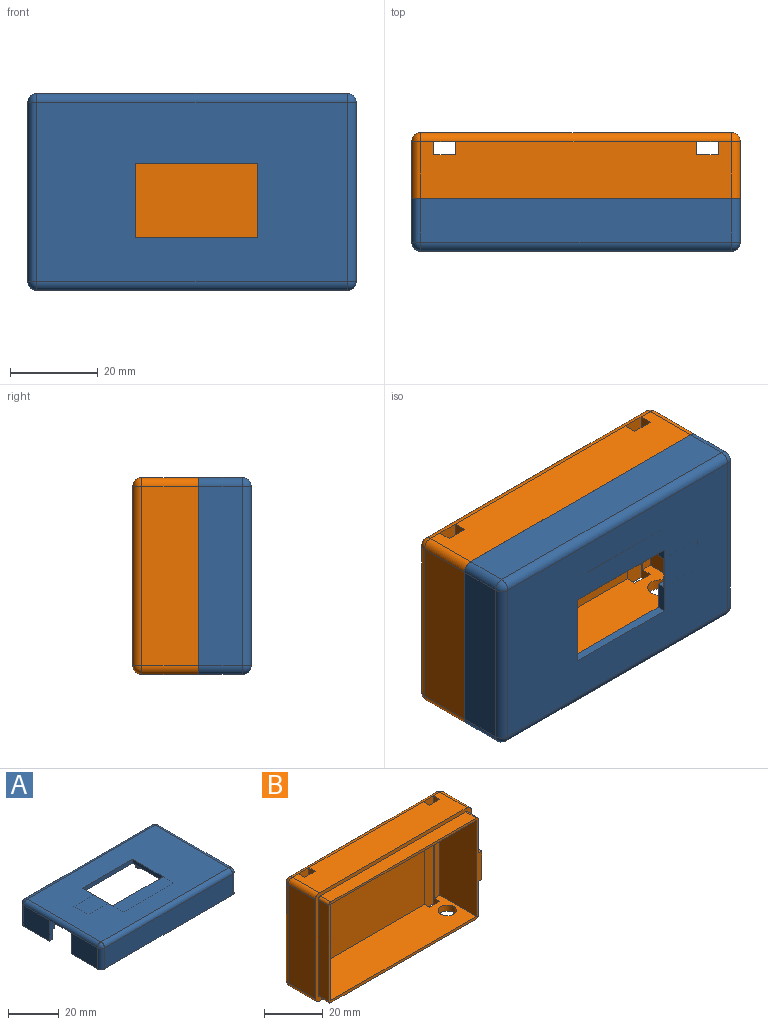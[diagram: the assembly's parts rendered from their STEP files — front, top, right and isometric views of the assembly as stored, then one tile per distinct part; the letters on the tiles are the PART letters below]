
ASSEMBLY  parts=2 mates=1
PART A: 55 faces, bbox 75x45x12 mm
  f0: cylinder r=2mm len=4mm, axis (0,0,1), area 37.7mm2, adj f12,f54
  f1: cylinder r=2mm len=4mm, axis (0,0,1), area 37.7mm2, adj f12,f53
  f2: cylinder r=2mm len=4mm, axis (0,0,1), area 37.7mm2, adj f12,f52
  f3: cylinder r=2mm len=4mm, axis (0,0,1), area 37.7mm2, adj f12,f51
  f4: plane 14x5mm, normal (1,0,0), area 70mm2, adj f7,f12,f40,f50
  f5: plane 75x45mm, normal (0,0,-1), area 309mm2, adj f10,f16,f17,f18,f19,f27,f29,f32
  f6: plane 14x5mm, normal (1,0,0), area 70mm2, adj f9,f12,f39,f50
  f7: plane 70x5mm, normal (0,1,0), area 350mm2, adj f4,f8,f12,f50
  f8: plane 40x5mm, normal (-1,0,0), area 200mm2, adj f7,f9,f12,f50
  f9: plane 70x5mm, normal (0,-1,0), area 350mm2, adj f6,f8,f12,f50
  f10: plane 14.5x10mm, normal (-1,0,0), area 145mm2, adj f5,f35,f38,f40
  f11: plane 28x0.2mm, normal (0,1,0), area 5.6mm2, adj f13,f15,f20,f26
  f12: plane 72.5x40mm, normal (0,0,-1), area 2047.7mm2, adj f0,f1,f2,f3,f4,f6,f7,f8
  f13: plane 23x2mm, normal (1,0,0), area 30.4mm2, adj f11,f12,f14,f20,f21,f22,f24,f25
  f14: plane 28x2mm, normal (0,-1,0), area 56mm2, adj f12,f13,f15,f20
  f15: plane 23x2mm, normal (-1,0,0), area 44.8mm2, adj f11,f12,f14,f20,f25,f26
  f16: plane 14.5x10mm, normal (-1,0,0), area 145mm2, adj f5,f29,f35,f39
  f17: plane 71x10mm, normal (0,-1,0), area 710mm2, adj f5,f32,f36,f38
  f18: plane 41x10mm, normal (1,0,0), area 410mm2, adj f5,f27,f31,f32
  f19: plane 71x10mm, normal (0,1,0), area 710mm2, adj f5,f27,f29,f30
  f20: plane 71x41mm, normal (0,0,1), area 2435mm2, adj f11,f13,f14,f15,f30,f31,f35,f36
  f21: plane 11x1.8mm, normal (0,-1,0), area 19.8mm2, adj f12,f13,f23,f24
  f22: plane 11x1.8mm, normal (0,1,0), area 19.8mm2, adj f12,f13,f23,f24
  f23: plane 8x1.8mm, normal (1,0,0), area 14.4mm2, adj f12,f21,f22,f24
  f24: plane 11x8mm, normal (0,0,-1), area 88mm2, adj f13,f21,f22,f23
  f25: plane 28x1.8mm, normal (0,1,0), area 50.4mm2, adj f12,f13,f15,f26
  f26: plane 28x6mm, normal (0,0,-1), area 168mm2, adj f11,f13,f15,f25
  f27: cylinder r=2mm len=10mm, axis (0,0,-1), area 31.4mm2, adj f5,f18,f19,f28
  f28: sphere r=2mm, area 6.3mm2, adj f27,f30,f31
  f29: cylinder r=2mm len=10mm, axis (0,0,1), area 31.4mm2, adj f5,f16,f19,f33
  f30: cylinder r=2mm len=71mm, axis (-1,0,0), area 223.1mm2, adj f19,f20,f28,f33
  f31: cylinder r=2mm len=41mm, axis (0,1,0), area 128.8mm2, adj f18,f20,f28,f34
  f32: cylinder r=2mm len=10mm, axis (0,0,1), area 31.4mm2, adj f5,f17,f18,f34
  f33: sphere r=2mm, area 6.3mm2, adj f29,f30,f35
  f34: sphere r=2mm, area 6.3mm2, adj f31,f32,f36
  f35: cylinder r=2mm len=41mm, axis (0,-1,0), area 128.8mm2, adj f10,f12,f16,f20,f33,f37
  f36: cylinder r=2mm len=71mm, axis (1,0,0), area 223.1mm2, adj f17,f20,f34,f37
  f37: sphere r=2mm, area 6.3mm2, adj f35,f36,f38
  f38: cylinder r=2mm len=10mm, axis (0,0,-1), area 31.4mm2, adj f5,f10,f17,f37
  f39: plane 10x2.5mm, normal (0,-1,0), area 19.5mm2, adj f5,f6,f12,f16,f41,f50
  f40: plane 10x2.5mm, normal (0,1,0), area 19.5mm2, adj f4,f5,f10,f12,f49,f50
  f41: plane 14x5mm, normal (1,0,0), area 70mm2, adj f5,f39,f42,f50
  f42: cylinder r=1.1mm len=5mm, axis (0,0,-1), area 8.6mm2, adj f5,f41,f43,f50
  f43: plane 70x5mm, normal (0,-1,0), area 350mm2, adj f5,f42,f44,f50
  f44: cylinder r=1.1mm len=5mm, axis (0,0,-1), area 8.6mm2, adj f5,f43,f45,f50
  f45: plane 40x5mm, normal (-1,0,0), area 200mm2, adj f5,f44,f46,f50
  f46: cylinder r=1.1mm len=5mm, axis (0,0,-1), area 8.6mm2, adj f5,f45,f47,f50
  f47: plane 70x5mm, normal (0,1,0), area 350mm2, adj f5,f46,f48,f50
  f48: cylinder r=1.1mm len=5mm, axis (0,0,-1), area 8.6mm2, adj f5,f47,f49,f50
  f49: plane 14x5mm, normal (1,0,0), area 70mm2, adj f5,f40,f48,f50
  f50: plane 72.2x42.2mm, normal (0,0,-1), area 232.6mm2, adj f4,f6,f7,f8,f9,f39,f40,f41
  f51: plane 4x4mm, normal (0,0,-1), area 12.6mm2, adj f3
  f52: plane 4x4mm, normal (0,0,-1), area 12.6mm2, adj f2
  f53: plane 4x4mm, normal (0,0,-1), area 12.6mm2, adj f1
  f54: plane 4x4mm, normal (0,0,-1), area 12.6mm2, adj f0
PART B: 48 faces, bbox 75x20x45 mm
  f0: plane 55x40mm, normal (0,-1,0), area 2200mm2, adj f7,f9,f28,f35
  f1: plane 40x2.5mm, normal (0,-1,0), area 100mm2, adj f7,f8,f9,f30
  f2: plane 71x13mm, normal (0,0,1), area 893mm2, adj f19,f26,f28,f30,f31,f33,f35,f36
  f3: plane 71x13mm, normal (0,0,-1), area 862.3mm2, adj f19,f25,f27,f28,f30,f32,f33,f35
  f4: plane 13.9x5mm, normal (1,0,0), area 69.5mm2, adj f5,f17,f19,f23
  f5: plane 73.5x42mm, normal (0,-1,0), area 241mm2, adj f4,f6,f7,f8,f9,f11,f12,f13
  f6: plane 40x17.5mm, normal (1,0,0), area 700mm2, adj f5,f7,f9,f10
  f7: plane 70x17.5mm, normal (0,0,1), area 1169.3mm2, adj f0,f1,f5,f6,f8,f10,f25,f27
  f8: plane 40x17.5mm, normal (-1,0,0), area 700mm2, adj f1,f5,f7,f9
  f9: plane 70x17.5mm, normal (0,0,-1), area 1200mm2, adj f0,f1,f5,f6,f8,f10,f26,f28
  f10: plane 40x2.5mm, normal (0,-1,0), area 100mm2, adj f6,f7,f9,f33
  f11: cylinder r=1.1mm len=5mm, axis (0,-1,0), area 8.6mm2, adj f5,f12,f18,f19
  f12: plane 39.8x5mm, normal (-1,0,0), area 199mm2, adj f5,f11,f13,f19
  f13: cylinder r=1.1mm len=5mm, axis (0,-1,0), area 8.6mm2, adj f5,f12,f14,f19
  f14: plane 69.8x5mm, normal (0,0,1), area 349mm2, adj f5,f13,f15,f19
  f15: cylinder r=1.1mm len=5mm, axis (0,-1,0), area 8.6mm2, adj f5,f14,f16,f19
  f16: plane 13.9x5mm, normal (1,0,0), area 69.5mm2, adj f5,f15,f19,f24
  f17: cylinder r=1.1mm len=5mm, axis (0,-1,0), area 8.6mm2, adj f4,f5,f18,f19
  f18: plane 69.8x5mm, normal (0,0,-1), area 349mm2, adj f5,f11,f17,f19
  f19: plane 75x45mm, normal (0,-1,0), area 330.6mm2, adj f2,f3,f4,f11,f12,f13,f14,f15
  f20: plane 71x41mm, normal (0,1,0), area 2911mm2, adj f39,f40,f44,f45
  f21: plane 41x18mm, normal (1,0,0), area 593mm2, adj f5,f19,f23,f24,f36,f38,f39
  f22: plane 41x13mm, normal (-1,0,0), area 533mm2, adj f19,f41,f45,f47
  f23: plane 5x1.5mm, normal (0,0,-1), area 7.5mm2, adj f4,f5,f19,f21
  f24: plane 5x1.5mm, normal (0,0,1), area 7.5mm2, adj f5,f16,f19,f21
  f25: cylinder r=3.12mm len=6.25mm, axis (0,0,-1), area 49.1mm2, adj f3,f7
  f26: plane 5x2.5mm, normal (0,1,0), area 12.5mm2, adj f2,f9,f28,f30
  f27: plane 5x2.5mm, normal (0,1,0), area 12.5mm2, adj f3,f7,f28,f30
  f28: plane 45x3mm, normal (1,0,0), area 35mm2, adj f0,f2,f3,f7,f9,f26,f27,f29
  f29: plane 45x5mm, normal (0,-1,0), area 225mm2, adj f28,f30,f40,f44
  f30: plane 45x3mm, normal (-1,0,0), area 35mm2, adj f1,f2,f3,f7,f9,f26,f27,f29
  f31: plane 5x2.5mm, normal (0,1,0), area 12.5mm2, adj f2,f9,f33,f35
  f32: plane 5x2.5mm, normal (0,1,0), area 12.5mm2, adj f3,f7,f33,f35
  f33: plane 45x3mm, normal (1,0,0), area 35mm2, adj f2,f3,f7,f9,f10,f31,f32,f34
  f34: plane 45x5mm, normal (0,-1,0), area 225mm2, adj f33,f35,f40,f44
  f35: plane 45x3mm, normal (-1,0,0), area 35mm2, adj f0,f2,f3,f7,f9,f31,f32,f34
  f36: cylinder r=2mm len=13mm, axis (0,-1,0), area 40.8mm2, adj f2,f19,f21,f37
  f37: sphere r=2mm, area 6.3mm2, adj f36,f39,f40
  f38: cylinder r=2mm len=13mm, axis (0,1,0), area 40.8mm2, adj f3,f19,f21,f42
  f39: cylinder r=2mm len=41mm, axis (0,0,1), area 128.8mm2, adj f20,f21,f37,f42
  f40: cylinder r=2mm len=71mm, axis (-1,0,0), area 223.1mm2, adj f2,f20,f29,f34,f37,f43
  f41: cylinder r=2mm len=13mm, axis (0,1,0), area 40.8mm2, adj f2,f19,f22,f43
  f42: sphere r=2mm, area 6.3mm2, adj f38,f39,f44
  f43: sphere r=2mm, area 6.3mm2, adj f40,f41,f45
  f44: cylinder r=2mm len=71mm, axis (1,0,0), area 223.1mm2, adj f3,f20,f29,f34,f42,f46
  f45: cylinder r=2mm len=41mm, axis (0,0,-1), area 128.8mm2, adj f20,f22,f43,f46
  f46: sphere r=2mm, area 6.3mm2, adj f44,f45,f47
  f47: cylinder r=2mm len=13mm, axis (0,-1,0), area 40.8mm2, adj f3,f19,f22,f46
PLACE A rot(axis=(0,0.71,-0.71),180deg) t=(51.91,-30.59,62.16)mm
PLACE B t=(-23.09,-3.59,17.16)mm fixed
MATE slider A.f20 <-> B.f0  axis (0,-1,0) through (14.21,-30.59,40.06)mm
